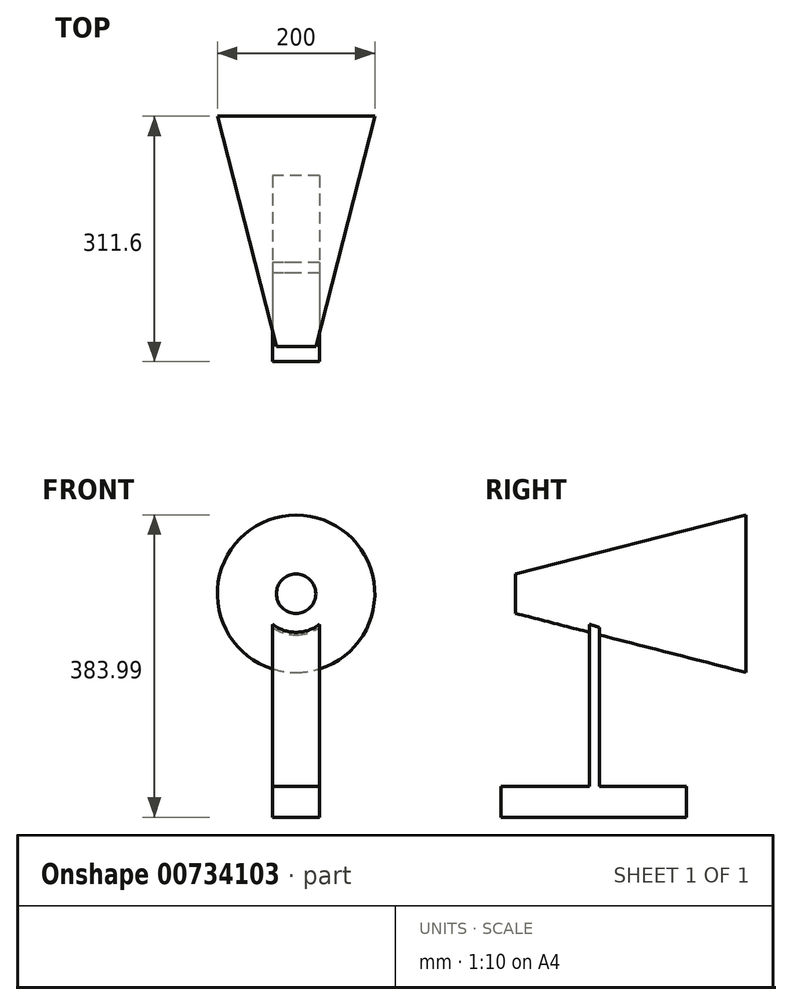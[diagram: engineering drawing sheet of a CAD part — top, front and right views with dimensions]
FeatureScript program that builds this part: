
annotation { "Feature Type Name" : "Feature", "Feature Type Description" : "" }
export const myFeature = defineFeature(function(context is Context, id is Id, definition is map)
    precondition{}
    {
        {
            var Q0;
            Q0=qCreatedBy(makeId("Right.planeOp"),FACE);
            var sketch = newSketch(context, id + "F0", { "sketchPlane" : qUnion([Q0])});
            skLineSegment(sketch, "E0.bottom", {"start": v(2.5, 100) * mm, "end": v(-2.5, 100) * mm});
            skLineSegment(sketch, "E0.top", {"start": v(2.5, -100) * mm, "end": v(-2.5, -100) * mm});
            skLineSegment(sketch, "E0.left", {"start": v(2.5, 100) * mm, "end": v(2.5, -100) * mm});
            skLineSegment(sketch, "E0.right", {"start": v(-2.5, 100) * mm, "end": v(-2.5, -100) * mm});
            skPoint(sketch, "E0.middle", {"position": v(0, 0) * mm});
            skLineSegment(sketch, "E1.bottom", {"start": v(-295.17, 25) * mm, "end": v(-304.83, 25) * mm});
            skLineSegment(sketch, "E1.top", {"start": v(-295.17, -25) * mm, "end": v(-304.83, -25) * mm});
            skLineSegment(sketch, "E1.left", {"start": v(-295.17, 25) * mm, "end": v(-295.17, -25) * mm});
            skLineSegment(sketch, "E1.right", {"start": v(-304.83, 25) * mm, "end": v(-304.83, -25) * mm});
            skPoint(sketch, "E1.middle", {"position": v(-300, 0) * mm});
            skLineSegment(sketch, "E2", {"start": v(-300, 0) * mm, "end": v(0, 0) * mm});
            skLineSegment(sketch, "E3", {"start": v(-295.17, 25) * mm, "end": v(-2.5, 100) * mm});
            skLineSegment(sketch, "E4", {"start": v(-295.17, -25) * mm, "end": v(-2.5, -100) * mm});
            skSolve(sketch);
        }
        {
            var Q0;
            {var subQ0=sQuery(id+"F0.wireOp",EDGE,"E3");Q0=makeQuery(id+"F0.imprint","IMPRINT",FACE,{"disambiguationData":[TD([[makeQuery(id+"F0.imprint","IMPRINT",EDGE,{"derivedFrom":subQ0}),-1.0]])]});}
            var Q1;
            Q1=sQuery(id+"F0.wireOp",EDGE,"E2");
            revolve(context, id + "F1", {"surfaceOperationType" : NewSurfaceOperationType.NEW, "entities" : qUnion([Q0]), "axis" : qUnion([Q1]), "revolveType" : RevolveType.FULL});
        }
        {
            var Q0;
            Q0=qCreatedBy(makeId("Right.planeOp"),FACE);
            var sketch = newSketch(context, id + "F2", { "sketchPlane" : qUnion([Q0])});
            skLineSegment(sketch, "E5.bottom", {"start": v(-201.46, 0) * mm, "end": v(-188.46, 0) * mm});
            skLineSegment(sketch, "E5.top", {"start": v(-201.46, -244.62) * mm, "end": v(-188.46, -244.62) * mm});
            skLineSegment(sketch, "E5.left", {"start": v(-201.46, 0) * mm, "end": v(-201.46, -244.62) * mm});
            skLineSegment(sketch, "E5.right", {"start": v(-188.46, 0) * mm, "end": v(-188.46, -244.62) * mm});
            skLineSegment(sketch, "E6.bottom", {"start": v(-78.03, -244.62) * mm, "end": v(-314.1, -244.62) * mm});
            skLineSegment(sketch, "E6.top", {"start": v(-78.03, -284) * mm, "end": v(-314.1, -284) * mm});
            skLineSegment(sketch, "E6.left", {"start": v(-78.03, -244.62) * mm, "end": v(-78.03, -284) * mm});
            skLineSegment(sketch, "E6.right", {"start": v(-314.1, -244.62) * mm, "end": v(-314.1, -284) * mm});
            skSolve(sketch);
        }
        {
            var Q0;
            Q0=makeQuery(id+"F2.imprint","IMPRINT",FACE,{"disambiguationData":[TD([[makeQuery(id+"F2.imprint","IMPRINT",EDGE,{"derivedFrom":sQuery(id+"F2.wireOp",EDGE,"E5.bottom")}),-1.0]])]});
            var Q1;
            Q1=makeQuery(id+"F2.imprint","IMPRINT",FACE,{"disambiguationData":[TD([[makeQuery(id+"F2.imprint","IMPRINT",EDGE,{"derivedFrom":sQuery(id+"F2.wireOp",EDGE,"E6.top")}),-1.0]])]});
            extrude(context, id + "F3", {"entities" : qUnion([Q0, Q1]), "operationType" : NewBodyOperationType.ADD, "endBound" : BoundingType.SYMMETRIC, "depth" : 60 * mm, "offsetDistance" : 25 * mm});
        }
    });
